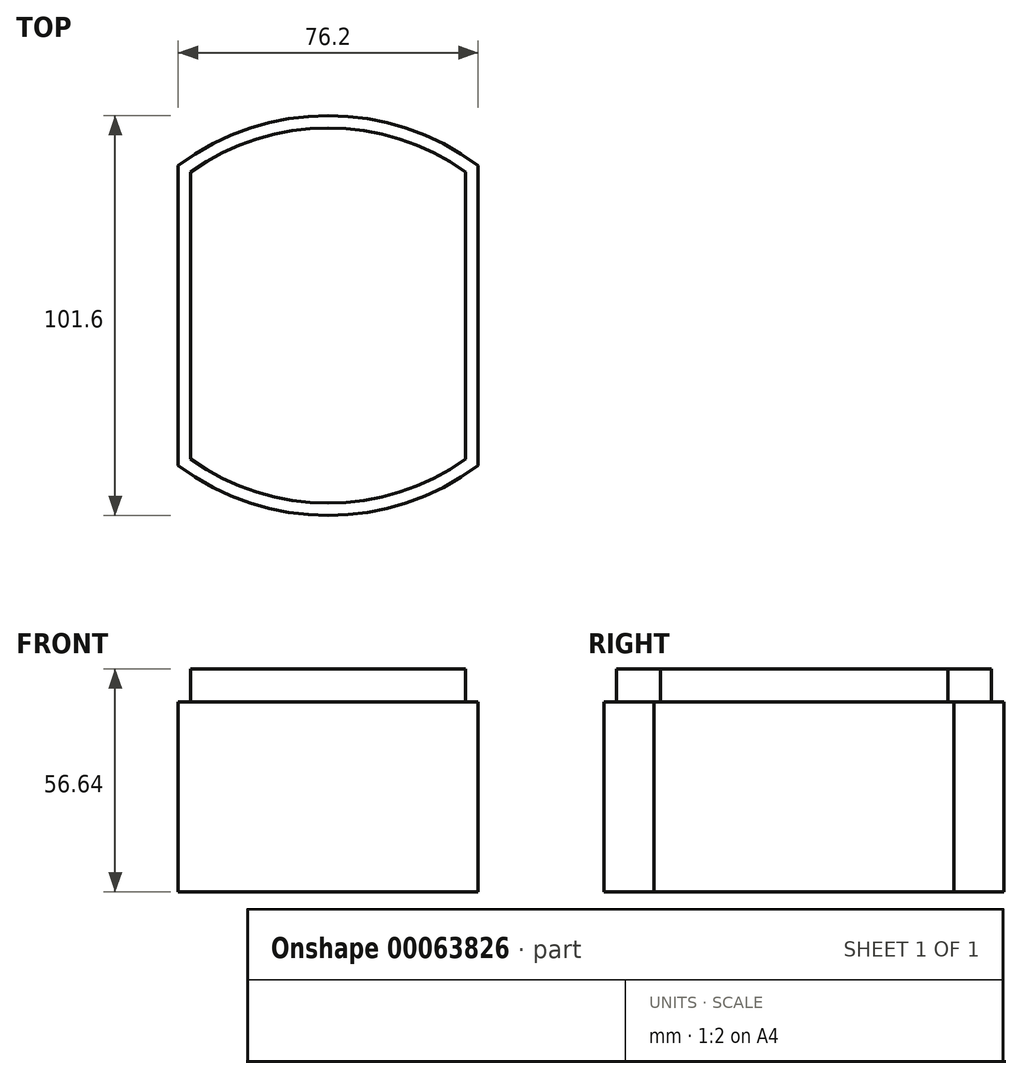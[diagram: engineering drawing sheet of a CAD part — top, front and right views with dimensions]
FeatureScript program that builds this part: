
annotation { "Feature Type Name" : "Feature", "Feature Type Description" : "" }
export const myFeature = defineFeature(function(context is Context, id is Id, definition is map)
    precondition{}
    {
        {
            var Q0;
            Q0=qCreatedBy(makeId("Top.planeOp"),FACE);
            var sketch = newSketch(context, id + "F0", { "sketchPlane" : qUnion([Q0])});
            skLineSegment(sketch, "E0.rect.bottom", {"start": v(38.1, -38.1) * mm, "end": v(-38.1, -38.1) * mm, "construction": true});
            skLineSegment(sketch, "E0.rect.top", {"start": v(38.1, 38.1) * mm, "end": v(-38.1, 38.1) * mm, "construction": true});
            skLineSegment(sketch, "E0.rect.left", {"start": v(38.1, -38.1) * mm, "end": v(38.1, 38.1) * mm});
            skLineSegment(sketch, "E0.rect.right", {"start": v(-38.1, -38.1) * mm, "end": v(-38.1, 38.1) * mm});
            skPoint(sketch, "E0.rect.middle", {"position": v(0, 0) * mm});
            skLineSegment(sketch, "E1", {"start": v(0, 38.1) * mm, "end": v(0, 50.8) * mm, "construction": true});
            skPoint(sketch, "E1.endSnap0", {"position": v(0, 38.1) * mm});
            skArc(sketch, "E2", {"start": v(38.1, 38.1) * mm, "mid": v(0, 50.8) * mm, "end": v(-38.1, 38.1) * mm});
            skLineSegment(sketch, "E3", {"start": v(-38.1, 0) * mm, "end": v(38.1, 0) * mm, "construction": true});
            skArc(sketch, "E4.MirrorCS", {"start": v(38.1, -38.1) * mm, "mid": v(0, -50.8) * mm, "end": v(-38.1, -38.1) * mm});
            skSolve(sketch);
        }
        {
            var Q0;
            Q0 = qSketchRegion(id + "F0", true);
            extrude(context, id + "F1", {"entities" : qUnion([Q0]), "oppositeDirection" : true, "depth" : 48.26 * mm});
        }
        {
            var Q0;
            Q0=makeQuery(id+"F0.imprint","IMPRINT",FACE,{"disambiguationData":[TD([[makeQuery(id+"F0.imprint","IMPRINT",EDGE,{"derivedFrom":sQuery(id+"F0.wireOp",EDGE,"E0.rect.left")}),1.0]])]});
            var sketch = newSketch(context, id + "F2", { "sketchPlane" : qUnion([Q0])});
            skLineSegment(sketch, "E5.0", {"start": v(-38.1, -38.1) * mm, "end": v(-38.1, 38.1) * mm, "construction": true});
            skArc(sketch, "E6.0", {"start": v(38.1, 38.1) * mm, "mid": v(0, 50.8) * mm, "end": v(-38.1, 38.1) * mm, "construction": true});
            skLineSegment(sketch, "E7.0", {"start": v(38.1, -38.1) * mm, "end": v(38.1, 38.1) * mm, "construction": true});
            skArc(sketch, "E8.0", {"start": v(38.1, -38.1) * mm, "mid": v(0, -50.8) * mm, "end": v(-38.1, -38.1) * mm, "construction": true});
            skLineSegment(sketch, "E9.0", {"start": v(-34.92, -36.49) * mm, "end": v(-34.92, 36.49) * mm});
            skArc(sketch, "E9.1", {"start": v(34.92, -36.49) * mm, "mid": v(0, -47.63) * mm, "end": v(-34.92, -36.49) * mm});
            skLineSegment(sketch, "E9.2", {"start": v(34.93, -36.49) * mm, "end": v(34.93, 36.49) * mm});
            skArc(sketch, "E9.3", {"start": v(34.93, 36.49) * mm, "mid": v(0, 47.62) * mm, "end": v(-34.92, 36.49) * mm});
            skSolve(sketch);
        }
        {
            var Q0;
            Q0 = qSketchRegion(id + "F2", true);
            extrude(context, id + "F3", {"entities" : qUnion([Q0]), "operationType" : NewBodyOperationType.ADD, "depth" : 8.38 * mm});
        }
    });
